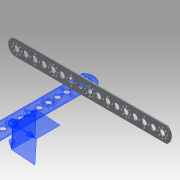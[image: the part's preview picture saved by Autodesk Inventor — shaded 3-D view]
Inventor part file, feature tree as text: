
AUTODESK INVENTOR PART (.ipt)
format: ipt  version: 2016 (Build 200138000, 138)  size: 234,496 bytes
history: native  units: in
note: dims shown in document units (in); Inventor stores cm internally (conversion verified against a paired STEP export)
features: sketch x4, extrude x3, hole x2, fillet x1, pattern_linear x1
ambient origin geometry x8: Origin, YZ Plane, XZ Plane, XY Plane, X Axis, Y Axis, Z Axis, Center Point
bodies: Solid1 (feature_tree)
feature tree (11):
  extrude  "Extrusion1"  Depth=1.063in
  extrude  "Extrusion2"  Depth=0.5315in
  fillet  "Fillet1"  Radius=0.562in
  hole  "Hole1"  [1 undecoded]
  pattern_linear  "Rectangular Pattern1"  Count1=17 Spacing1=0.6193in
  hole  "Hole2"  [1 undecoded]
  extrude  "Extrusion3"  Depth=0.5315in
  sketch  "Sketch1"  dims[d0=11.3386in d1=1.063in]
  sketch  "Sketch2"  dims[d2=0.0803in d3=0.0in d4=0.5315in d5=0.562in]
  sketch  "Sketch3"  dims[d6=0.0in d7=0.3839in]
  sketch  "Sketch5"  dims[d8=0.1in d11=6.6929in d13=0.6193in d14=0.3937in d16=1.0in d18=0.0803in d19=0.0in d20=0.5315in d28=3.1496in d30=360.0deg d32=0.1469in d33=0.75in d34=0.375in d35=0.25in d36=0.5635in d37=1.0in d38=0.8108in d39=0.3096in d40=1.9685in d42=2.4772in d43=0.3096in d44=1.5748in d46=360.0deg d48=0.0in d49=0.6134in d50=1.5748in d52=2.4772in d53=0.3937in d55=1.0in d57=0.1469in d58=0.75in d59=0.375in d60=0.25in d61=0.5635in d62=1.0in d63=0.8108in d64=1.0in d65=0.0in]
note: 2 required parameter values undecoded (feature->parameter linkage not recoverable at this tier; creation-order binding heuristic only, values carry confidence <= 0.55)
